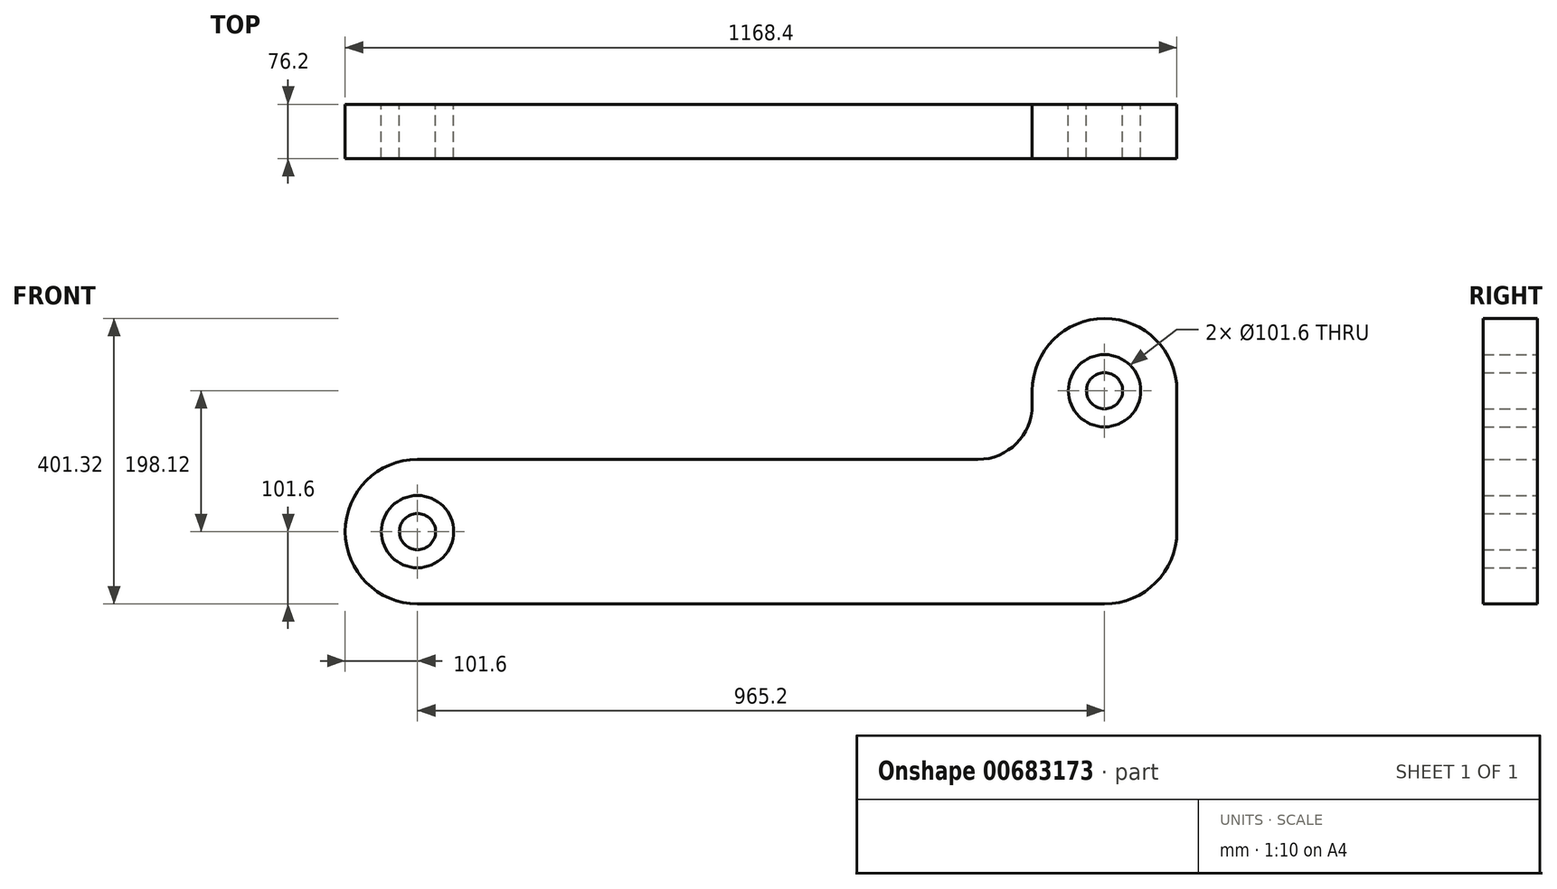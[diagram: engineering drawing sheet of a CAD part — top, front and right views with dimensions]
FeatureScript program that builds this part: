
annotation { "Feature Type Name" : "Feature", "Feature Type Description" : "" }
export const myFeature = defineFeature(function(context is Context, id is Id, definition is map)
    precondition{}
    {
        {
            var Q0;
            Q0=qCreatedBy(makeId("Front.planeOp"),FACE);
            var sketch = newSketch(context, id + "F0", { "sketchPlane" : qUnion([Q0])});
            skArc(sketch, "E0", {"start": v(0, 101.6) * mm, "mid": v(-101.6, 0) * mm, "end": v(0, -101.6) * mm});
            skArc(sketch, "E1", {"start": v(965.2, -101.6) * mm, "mid": v(1037.04, -71.84) * mm, "end": v(1066.8, 0) * mm});
            skLineSegment(sketch, "E2", {"start": v(0, 101.6) * mm, "end": v(787.4, 101.6) * mm});
            skLineSegment(sketch, "E3", {"start": v(0, -101.6) * mm, "end": v(965.2, -101.6) * mm});
            skCircle(sketch, "E4", {"center": v(0, 0) * mm, "radius": 50.8 * mm});
            skCircle(sketch, "E5", {"center": v(965.2, 0) * mm, "radius": 50.8 * mm});
            skLineSegment(sketch, "E6", {"start": v(965.2, 0) * mm, "end": v(965.2, 198.12) * mm});
            skCircle(sketch, "E7", {"center": v(965.2, 198.12) * mm, "radius": 50.8 * mm});
            skArc(sketch, "E8", {"start": v(1066.8, 198.12) * mm, "mid": v(965.2, 299.72) * mm, "end": v(863.6, 198.12) * mm});
            skLineSegment(sketch, "E9", {"start": v(1066.8, 198.12) * mm, "end": v(1066.8, 0) * mm});
            skLineSegment(sketch, "E10", {"start": v(863.6, 198.12) * mm, "end": v(863.6, 177.8) * mm});
            skPoint(sketch, "E11.visualSharp", {"position": v(863.6, 101.6) * mm});
            skArc(sketch, "E11.filletArc", {"start": v(787.4, 101.6) * mm, "mid": v(841.28, 123.92) * mm, "end": v(863.6, 177.8) * mm});
            skCircle(sketch, "E12", {"center": v(965.2, 198.12) * mm, "radius": 25.4 * mm});
            skCircle(sketch, "E13", {"center": v(965.2, 0) * mm, "radius": 25.4 * mm});
            skCircle(sketch, "E14", {"center": v(0, 0) * mm, "radius": 25.4 * mm});
            skSolve(sketch);
        }
        {
            var Q0;
            Q0 = qSketchRegion(id + "F0", true);
            var Q1;
            Q1=makeQuery(id+"F0.imprint","IMPRINT",FACE,{"disambiguationData":[TD([[makeQuery(id+"F0.imprint","IMPRINT",EDGE,{"derivedFrom":sQuery(id+"F0.wireOp",EDGE,"E14")}),1.0]])]});
            var Q2;
            Q2=makeQuery(id+"F0.imprint","IMPRINT",FACE,{"disambiguationData":[TD([[makeQuery(id+"F0.imprint","IMPRINT",EDGE,{"derivedFrom":sQuery(id+"F0.wireOp",EDGE,"E13")}),1.0]])]});
            var Q3;
            Q3=makeQuery(id+"F0.imprint","IMPRINT",FACE,{"disambiguationData":[TD([[makeQuery(id+"F0.imprint","IMPRINT",EDGE,{"derivedFrom":sQuery(id+"F0.wireOp",EDGE,"E12")}),1.0]])]});
            var Q4;
            Q4=makeQuery(id+"F0.imprint","IMPRINT",FACE,{"disambiguationData":[TD([[makeQuery(id+"F0.imprint","IMPRINT",EDGE,{"derivedFrom":sQuery(id+"F0.wireOp",EDGE,"E5")}),1.0]])]});
            extrude(context, id + "F1", {"entities" : qUnion([Q0, Q1, Q2, Q3, Q4]), "depth" : 76.2 * mm, "offsetDistance" : 25.4 * mm});
        }
    });
